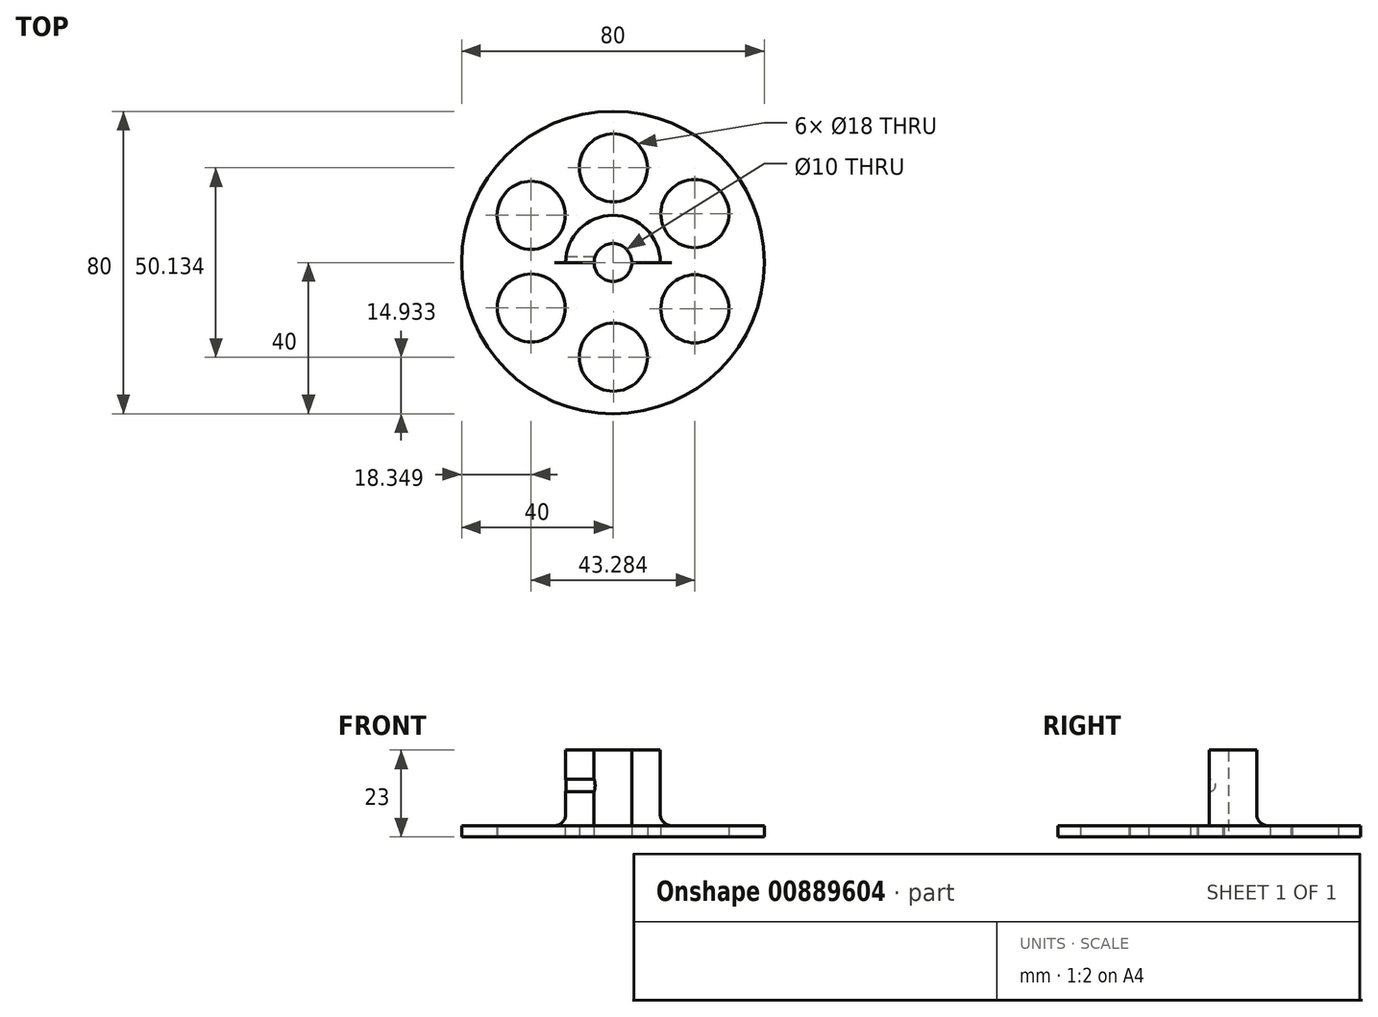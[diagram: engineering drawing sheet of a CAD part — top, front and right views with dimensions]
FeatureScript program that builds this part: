
annotation { "Feature Type Name" : "Feature", "Feature Type Description" : "" }
export const myFeature = defineFeature(function(context is Context, id is Id, definition is map)
    precondition{}
    {
        {
            var Q0;
            Q0=qCreatedBy(makeId("Top.planeOp"),FACE);
            var sketch = newSketch(context, id + "F0", { "sketchPlane" : qUnion([Q0])});
            skCircle(sketch, "E0", {"center": v(0, 0) * mm, "radius": 40 * mm});
            skArc(sketch, "E1", {"start": v(12.5, 0) * mm, "mid": v(0, 12.5) * mm, "end": v(-12.5, 0) * mm});
            skArc(sketch, "E2", {"start": v(5, 0) * mm, "mid": v(0, 5) * mm, "end": v(-5, 0) * mm});
            skLineSegment(sketch, "E3", {"start": v(-12.5, 0) * mm, "end": v(-5, 0) * mm});
            skLineSegment(sketch, "E4", {"start": v(5, 0) * mm, "end": v(12.5, 0) * mm});
            skCircle(sketch, "E5", {"center": v(0, 0) * mm, "radius": 5 * mm});
            skCircle(sketch, "E6", {"center": v(0, 0) * mm, "radius": 25 * mm, "construction": true});
            skLineSegment(sketch, "E7", {"start": v(0, 0) * mm, "end": v(-48.39, 27.94) * mm, "construction": true});
            skLineSegment(sketch, "E8", {"start": v(0, 0) * mm, "end": v(40.52, 23.4) * mm, "construction": true});
            skLineSegment(sketch, "E9", {"start": v(0, 0) * mm, "end": v(40.52, -23.4) * mm, "construction": true});
            skLineSegment(sketch, "E10", {"start": v(0, 0) * mm, "end": v(-41.8, -24.14) * mm, "construction": true});
            skPoint(sketch, "E11", {"position": v(-21.65, 12.5) * mm});
            skPoint(sketch, "E12", {"position": v(0, 25) * mm});
            skPoint(sketch, "E13", {"position": v(21.65, 12.5) * mm});
            skPoint(sketch, "E14", {"position": v(21.65, -12.5) * mm});
            skPoint(sketch, "E15", {"position": v(0, -25) * mm});
            skPoint(sketch, "E16", {"position": v(-21.65, -12.5) * mm});
            skCircle(sketch, "E17", {"center": v(-21.65, 12.5) * mm, "radius": 9 * mm});
            skCircle(sketch, "E18", {"center": v(0.11, 25.07) * mm, "radius": 9 * mm});
            skCircle(sketch, "E19", {"center": v(21.63, 12.93) * mm, "radius": 9 * mm});
            skCircle(sketch, "E20", {"center": v(21.63, -12.25) * mm, "radius": 9 * mm});
            skCircle(sketch, "E21", {"center": v(0.11, -25.07) * mm, "radius": 9 * mm});
            skCircle(sketch, "E22", {"center": v(-21.63, -12.02) * mm, "radius": 9 * mm});
            skSolve(sketch);
        }
        {
            var Q0;
            Q0=makeQuery(id+"F0.imprint","IMPRINT",FACE,{"disambiguationData":[TD([[makeQuery(id+"F0.imprint","IMPRINT",EDGE,{"derivedFrom":sQuery(id+"F0.wireOp",EDGE,"E0")}),1.0]])]});
            var Q1;
            Q1=makeQuery(id+"F0.imprint","IMPRINT",FACE,{"disambiguationData":[TD([[makeQuery(id+"F0.imprint","IMPRINT",EDGE,{"derivedFrom":sQuery(id+"F0.wireOp",EDGE,"E1")}),1.0]])]});
            extrude(context, id + "F1", {"entities" : qUnion([Q0, Q1]), "depth" : 3 * mm, "offsetDistance" : 25 * mm});
        }
        {
            var Q0;
            Q0=makeQuery(id+"F0.imprint","IMPRINT",FACE,{"disambiguationData":[TD([[makeQuery(id+"F0.imprint","IMPRINT",EDGE,{"derivedFrom":sQuery(id+"F0.wireOp",EDGE,"E1")}),1.0]])]});
            extrude(context, id + "F2", {"entities" : qUnion([Q0]), "operationType" : NewBodyOperationType.ADD, "depth" : 18 * mm, "offsetDistance" : 25 * mm});
        }
        {
            var Q0;
            Q0 = qSketchRegion(id + "F0", true);
            extrude(context, id + "F3", {"entities" : qUnion([Q0]), "operationType" : NewBodyOperationType.REMOVE, "oppositeDirection" : true, "depth" : 25 * mm, "offsetDistance" : 25 * mm});
        }
        {
            var Q0;
            Q0=makeQuery(id+"F2.boolean.opBoolean","INTERSECT",EDGE,{"derivedFrom":[makeQuery(id+"F1.opExtrude","CAP_FACE",FACE,{"disambiguationData":[OSD([sQuery(id+"F0.wireOp",EDGE,"E0"),sQuery(id+"F0.wireOp",EDGE,"E5"),sQuery(id+"F0.wireOp",EDGE,"E17"),sQuery(id+"F0.wireOp",EDGE,"E18"),sQuery(id+"F0.wireOp",EDGE,"E19"),sQuery(id+"F0.wireOp",EDGE,"E20"),sQuery(id+"F0.wireOp",EDGE,"E21"),sQuery(id+"F0.wireOp",EDGE,"E22")])],"isStart":false}),makeQuery(id+"F2.opExtrude","SWEPT_FACE",FACE,{"disambiguationData":[OSD([sQuery(id+"F0.wireOp",EDGE,"E1")])]})]});
            fillet(context, id + "F4", {"entities" : qUnion([Q0]), "radius" : 3 * mm, "tangentPropagation" : true, "allowEdgeOverflow" : false});
        }
        {
            var Q0;
            Q0=qCreatedBy(makeId("Right.planeOp"),FACE);
            var sketch = newSketch(context, id + "F5", { "sketchPlane" : qUnion([Q0])});
            skCircle(sketch, "E23", {"center": v(0, 13.65) * mm, "radius": 1.61 * mm});
            skSolve(sketch);
        }
        {
            var Q0;
            Q0=makeQuery(id+"F5.imprint","IMPRINT",FACE,{"disambiguationData":[TD([[makeQuery(id+"F5.imprint","IMPRINT",EDGE,{"derivedFrom":sQuery(id+"F5.wireOp",EDGE,"E23")}),1.0]])]});
            extrude(context, id + "F6", {"entities" : qUnion([Q0]), "operationType" : NewBodyOperationType.REMOVE, "oppositeDirection" : true, "depth" : 40 * mm, "offsetDistance" : 25 * mm});
        }
        {
            var Q0;
            Q0=makeQuery(id+"F2.opExtrude","CAP_FACE",FACE,{"disambiguationData":[OSD([sQuery(id+"F0.wireOp",EDGE,"E1"),sQuery(id+"F0.wireOp",EDGE,"E3"),sQuery(id+"F0.wireOp",EDGE,"E4"),sQuery(id+"F0.wireOp",EDGE,"E5")])],"isStart":false});
            extrude(context, id + "F7", {"entities" : qUnion([Q0]), "operationType" : NewBodyOperationType.ADD, "depth" : 5 * mm, "offsetDistance" : 25 * mm});
        }
    });
